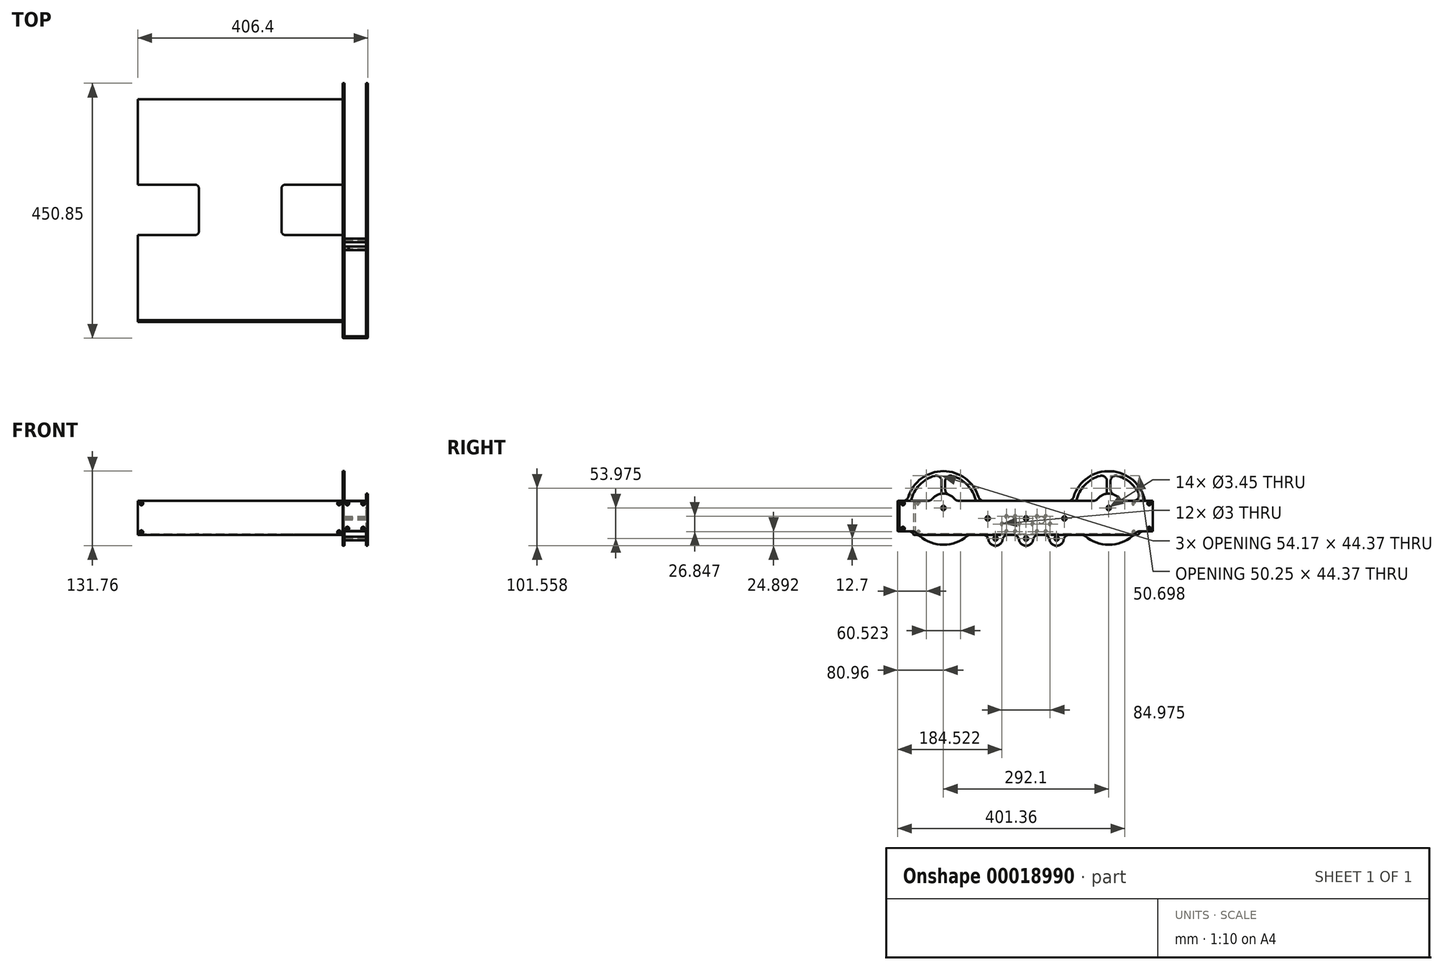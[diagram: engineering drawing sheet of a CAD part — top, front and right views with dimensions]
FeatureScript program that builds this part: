
annotation { "Feature Type Name" : "Feature", "Feature Type Description" : "" }
export const myFeature = defineFeature(function(context is Context, id is Id, definition is map)
    precondition{}
    {
        {
            var Q0;
            Q0=qCreatedBy(makeId("Right.planeOp"),FACE);
            var sketch = newSketch(context, id + "F0", { "sketchPlane" : qUnion([Q0])});
            skLineSegment(sketch, "E0", {"start": v(-222.25, 0) * mm, "end": v(222.25, 0) * mm});
            skCircle(sketch, "E1", {"center": v(-146.05, 79.38) * mm, "radius": 76.2 * mm});
            skCircle(sketch, "E2", {"center": v(-53.98, 25.4) * mm, "radius": 25.4 * mm});
            skCircle(sketch, "E3", {"center": v(53.98, 25.4) * mm, "radius": 25.4 * mm});
            skCircle(sketch, "E4", {"center": v(146.05, 79.38) * mm, "radius": 76.2 * mm});
            skLineSegment(sketch, "E5", {"start": v(0, 0) * mm, "end": v(0, 444.5) * mm, "construction": true});
            skLineSegment(sketch, "E6", {"start": v(222.25, 0) * mm, "end": v(222.25, 444.5) * mm, "construction": true});
            skCircle(sketch, "E7", {"center": v(0, 25.4) * mm, "radius": 25.4 * mm});
            skCircle(sketch, "E8", {"center": v(-146.05, 79.38) * mm, "radius": 63.5 * mm, "construction": true});
            skCircle(sketch, "E9", {"center": v(-53.98, 25.4) * mm, "radius": 21.17 * mm, "construction": true});
            skCircle(sketch, "E10", {"center": v(0, 25.4) * mm, "radius": 21.17 * mm, "construction": true});
            skCircle(sketch, "E11", {"center": v(53.98, 25.4) * mm, "radius": 21.17 * mm, "construction": true});
            skCircle(sketch, "E12", {"center": v(-67.76, 60.92) * mm, "radius": 16.93 * mm, "construction": true});
            skCircle(sketch, "E13", {"center": v(146.05, 79.38) * mm, "radius": 63.5 * mm, "construction": true});
            skCircle(sketch, "E14", {"center": v(-26.99, 58.02) * mm, "radius": 21.17 * mm, "construction": true});
            skCircle(sketch, "E15", {"center": v(26.99, 58.02) * mm, "radius": 21.17 * mm, "construction": true});
            skCircle(sketch, "E16", {"center": v(-67.76, 60.92) * mm, "radius": 3.18 * mm, "construction": true});
            skCircle(sketch, "E17", {"center": v(-67.76, 60.92) * mm, "radius": 18 * mm, "construction": true});
            skCircle(sketch, "E18", {"center": v(-26.99, 58.02) * mm, "radius": 22.23 * mm, "construction": true});
            skCircle(sketch, "E19", {"center": v(67.76, 60.92) * mm, "radius": 16.93 * mm, "construction": true});
            skLineSegment(sketch, "E20", {"start": v(-222.25, 0) * mm, "end": v(-222.25, 444.5) * mm, "construction": true});
            skSolve(sketch);
        }
        {
            var Q0;
            Q0=qCreatedBy(makeId("Right.planeOp"),FACE);
            var sketch = newSketch(context, id + "F1", { "sketchPlane" : qUnion([Q0])});
            skPoint(sketch, "E21.0", {"position": v(-146.05, 79.38) * mm});
            skPoint(sketch, "E21.1", {"position": v(-53.98, 25.4) * mm});
            skPoint(sketch, "E21.2", {"position": v(0, 25.4) * mm});
            skPoint(sketch, "E21.3", {"position": v(53.98, 25.4) * mm});
            skPoint(sketch, "E21.4", {"position": v(146.05, 79.38) * mm});
            skPoint(sketch, "E21.5", {"position": v(67.76, 60.92) * mm});
            skPoint(sketch, "E21.6", {"position": v(26.99, 58.02) * mm});
            skPoint(sketch, "E21.7", {"position": v(-26.99, 58.02) * mm});
            skPoint(sketch, "E21.8", {"position": v(-67.76, 60.92) * mm});
            skArc(sketch, "E22", {"start": v(42.98, 31.75) * mm, "mid": v(53.98, 12.7) * mm, "end": v(64.97, 31.75) * mm});
            skArc(sketch, "E23", {"start": v(-11, 31.75) * mm, "mid": v(0, 12.7) * mm, "end": v(11, 31.75) * mm});
            skArc(sketch, "E24", {"start": v(-64.97, 31.75) * mm, "mid": v(-53.98, 12.7) * mm, "end": v(-42.98, 31.75) * mm});
            skLineSegment(sketch, "E25", {"start": v(42.98, 31.75) * mm, "end": v(11, 31.75) * mm});
            skLineSegment(sketch, "E26", {"start": v(-11, 31.75) * mm, "end": v(-42.98, 31.75) * mm});
            skPoint(sketch, "E27", {"position": v(0, 60.92) * mm});
            skLineSegment(sketch, "E28", {"start": v(101.69, 31.75) * mm, "end": v(64.97, 31.75) * mm});
            skLineSegment(sketch, "E29", {"start": v(-198.44, 38.1) * mm, "end": v(-223.84, 38.1) * mm});
            skLineSegment(sketch, "E30", {"start": v(-223.84, 38.1) * mm, "end": v(-223.84, 92.08) * mm});
            skLineSegment(sketch, "E31", {"start": v(198.44, 38.1) * mm, "end": v(223.84, 38.1) * mm});
            skLineSegment(sketch, "E32", {"start": v(223.84, 38.1) * mm, "end": v(223.84, 92.08) * mm});
            skArc(sketch, "E33.trimOffspring", {"start": v(-190.41, 31.75) * mm, "mid": v(-146.05, 14.29) * mm, "end": v(-101.69, 31.75) * mm});
            skLineSegment(sketch, "E34.trimOffspring", {"start": v(-223.84, 92.08) * mm, "end": v(-168.05, 92.08) * mm});
            skCircle(sketch, "E35", {"center": v(0, 25.4) * mm, "radius": 3.9 * mm, "construction": true});
            skLineSegment(sketch, "E36.trimOffspring", {"start": v(-64.97, 31.75) * mm, "end": v(-101.69, 31.75) * mm});
            skArc(sketch, "E37.trimOffspring", {"start": v(101.69, 31.75) * mm, "mid": v(146.05, 14.29) * mm, "end": v(190.41, 31.75) * mm});
            skArc(sketch, "E38", {"start": v(-124.05, 92.08) * mm, "mid": v(-146.05, 104.78) * mm, "end": v(-168.05, 92.08) * mm});
            skArc(sketch, "E39", {"start": v(168.05, 92.08) * mm, "mid": v(146.05, 104.78) * mm, "end": v(124.05, 92.08) * mm});
            skLineSegment(sketch, "E40.trimOffspring", {"start": v(-124.05, 92.08) * mm, "end": v(124.05, 92.08) * mm});
            skLineSegment(sketch, "E41.trimOffspring", {"start": v(168.05, 92.08) * mm, "end": v(223.84, 92.08) * mm});
            skLineSegment(sketch, "E42", {"start": v(-190.41, 31.75) * mm, "end": v(-198.44, 31.75) * mm});
            skLineSegment(sketch, "E43", {"start": v(-198.44, 31.75) * mm, "end": v(-198.44, 38.1) * mm});
            skLineSegment(sketch, "E44", {"start": v(190.41, 31.75) * mm, "end": v(198.44, 31.75) * mm});
            skLineSegment(sketch, "E45", {"start": v(198.44, 31.75) * mm, "end": v(198.44, 38.1) * mm});
            skSolve(sketch);
        }
        {
            var Q0;
            Q0 = qSketchRegion(id + "F1", true);
            extrude(context, id + "F2", {"entities" : qUnion([Q0]), "depth" : 3.17 * mm});
        }
        {
            var Q0;
            Q0=makeQuery(id+"F2.opExtrude","SWEPT_EDGE",EDGE,{"disambiguationData":[OSD([sQuery(id+"F1.wireOp",EDGE,"E28"),sQuery(id+"F1.wireOp",EDGE,"E37.trimOffspring")])]});
            var Q1;
            Q1=makeQuery(id+"F2.opExtrude","SWEPT_EDGE",EDGE,{"disambiguationData":[OSD([sQuery(id+"F1.wireOp",EDGE,"E31"),sQuery(id+"F1.wireOp",EDGE,"E45")])]});
            var Q2;
            Q2=makeQuery(id+"F2.opExtrude","SWEPT_EDGE",EDGE,{"disambiguationData":[OSD([sQuery(id+"F1.wireOp",EDGE,"E37.trimOffspring"),sQuery(id+"F1.wireOp",EDGE,"E44")])]});
            var Q3;
            Q3=makeQuery(id+"F2.opExtrude","SWEPT_EDGE",EDGE,{"disambiguationData":[OSD([sQuery(id+"F1.wireOp",EDGE,"E24"),sQuery(id+"F1.wireOp",EDGE,"E36.trimOffspring")])]});
            var Q4;
            Q4=makeQuery(id+"F2.opExtrude","SWEPT_EDGE",EDGE,{"disambiguationData":[OSD([sQuery(id+"F1.wireOp",EDGE,"E24"),sQuery(id+"F1.wireOp",EDGE,"E26")])]});
            var Q5;
            Q5=makeQuery(id+"F2.opExtrude","SWEPT_EDGE",EDGE,{"disambiguationData":[OSD([sQuery(id+"F1.wireOp",EDGE,"E24"),sQuery(id+"F1.wireOp",EDGE,"E26")])]});
            var Q6;
            Q6=makeQuery(id+"F2.opExtrude","SWEPT_EDGE",EDGE,{"disambiguationData":[OSD([sQuery(id+"F1.wireOp",EDGE,"E23"),sQuery(id+"F1.wireOp",EDGE,"E26")])]});
            var Q7;
            Q7=makeQuery(id+"F2.opExtrude","SWEPT_EDGE",EDGE,{"disambiguationData":[OSD([sQuery(id+"F1.wireOp",EDGE,"E23"),sQuery(id+"F1.wireOp",EDGE,"E25")])]});
            var Q8;
            Q8=makeQuery(id+"F2.opExtrude","SWEPT_EDGE",EDGE,{"disambiguationData":[OSD([sQuery(id+"F1.wireOp",EDGE,"E22"),sQuery(id+"F1.wireOp",EDGE,"E25")])]});
            var Q9;
            Q9=makeQuery(id+"F2.opExtrude","SWEPT_EDGE",EDGE,{"disambiguationData":[OSD([sQuery(id+"F1.wireOp",EDGE,"E22"),sQuery(id+"F1.wireOp",EDGE,"E28")])]});
            var Q10;
            Q10=makeQuery(id+"F2.opExtrude","SWEPT_EDGE",EDGE,{"disambiguationData":[OSD([sQuery(id+"F1.wireOp",EDGE,"E22"),sQuery(id+"F1.wireOp",EDGE,"E25")])]});
            var Q11;
            Q11=makeQuery(id+"F2.opExtrude","SWEPT_EDGE",EDGE,{"disambiguationData":[OSD([sQuery(id+"F1.wireOp",EDGE,"E33.trimOffspring"),sQuery(id+"F1.wireOp",EDGE,"E36.trimOffspring")])]});
            var Q12;
            Q12=makeQuery(id+"F2.opExtrude","SWEPT_EDGE",EDGE,{"disambiguationData":[OSD([sQuery(id+"F1.wireOp",EDGE,"E29"),sQuery(id+"F1.wireOp",EDGE,"E43")])]});
            var Q13;
            Q13=makeQuery(id+"F2.opExtrude","SWEPT_EDGE",EDGE,{"disambiguationData":[OSD([sQuery(id+"F1.wireOp",EDGE,"E33.trimOffspring"),sQuery(id+"F1.wireOp",EDGE,"E42")])]});
            var Q14;
            Q14=makeQuery(id+"F2.opExtrude","SWEPT_EDGE",EDGE,{"disambiguationData":[OSD([sQuery(id+"F1.wireOp",EDGE,"E33.trimOffspring"),sQuery(id+"F1.wireOp",EDGE,"E36.trimOffspring")])]});
            var Q15;
            Q15=makeQuery(id+"F2.opExtrude","SWEPT_EDGE",EDGE,{"disambiguationData":[OSD([sQuery(id+"F1.wireOp",EDGE,"E28"),sQuery(id+"F1.wireOp",EDGE,"E37.trimOffspring")])]});
            var Q16;
            Q16=makeQuery(id+"F2.opExtrude","SWEPT_EDGE",EDGE,{"disambiguationData":[OSD([sQuery(id+"F1.wireOp",EDGE,"E34.trimOffspring"),sQuery(id+"F1.wireOp",EDGE,"E38")])]});
            var Q17;
            Q17=makeQuery(id+"F2.opExtrude","SWEPT_EDGE",EDGE,{"disambiguationData":[OSD([sQuery(id+"F1.wireOp",EDGE,"E38"),sQuery(id+"F1.wireOp",EDGE,"E40.trimOffspring")])]});
            var Q18;
            Q18=makeQuery(id+"F2.opExtrude","SWEPT_EDGE",EDGE,{"disambiguationData":[OSD([sQuery(id+"F1.wireOp",EDGE,"E39"),sQuery(id+"F1.wireOp",EDGE,"E40.trimOffspring")])]});
            var Q19;
            Q19=makeQuery(id+"F2.opExtrude","SWEPT_EDGE",EDGE,{"disambiguationData":[OSD([sQuery(id+"F1.wireOp",EDGE,"E39"),sQuery(id+"F1.wireOp",EDGE,"E41.trimOffspring")])]});
            fillet(context, id + "F3", {"entities" : qUnion([Q0, Q1, Q2, Q3, Q4, Q5, Q6, Q7, Q8, Q9, Q10, Q11, Q12, Q13, Q14, Q15, Q16, Q17, Q18, Q19]), "radius" : 9.52 * mm, "tangentPropagation" : true, "allowEdgeOverflow" : false});
        }
        {
            var Q0;
            Q0=sQuery(id+"F0.wireOp",VERTEX,"E1.center");
            var Q1;
            Q1=sQuery(id+"F0.wireOp",VERTEX,"E16.center");
            var Q2;
            Q2=sQuery(id+"F0.wireOp",VERTEX,"E2.center");
            var Q3;
            Q3=sQuery(id+"F0.wireOp",VERTEX,"E7.center");
            var Q4;
            Q4=sQuery(id+"F0.wireOp",VERTEX,"E11.center");
            var Q5;
            Q5=sQuery(id+"F0.wireOp",VERTEX,"E13.center");
            var Q6;
            Q6=sQuery(id+"F0.wireOp",VERTEX,"E19.center");
            var Q7;
            Q7=sQuery(id+"F1.wireOp",VERTEX,"E27");
            var Q8;
            Q8=makeQuery(id+"F2.opExtrude","SWEPT_BODY",BODY,{"disambiguationData":[OSD([sQuery(id+"F1.wireOp",EDGE,"15da93e0-f6f9-46fd-b5b2-a4333d812dff"),sQuery(id+"F1.wireOp",EDGE,"16e28298-e9de-4e3e-a815-65364f24cef6"),sQuery(id+"F1.wireOp",EDGE,"E22"),sQuery(id+"F1.wireOp",EDGE,"E23"),sQuery(id+"F1.wireOp",EDGE,"E24"),sQuery(id+"F1.wireOp",EDGE,"E25"),sQuery(id+"F1.wireOp",EDGE,"E26"),sQuery(id+"F1.wireOp",EDGE,"859b3a9e-47a0-477d-ad96-80d0cd043ae0"),sQuery(id+"F1.wireOp",EDGE,"689f9d55-c2b5-4ecb-a3d1-7254dc2b26e6"),sQuery(id+"F1.wireOp",EDGE,"4789f967-c616-4e3b-9a4c-ef86a0a08756")])]});
            hole(context, id + "F4", {"style" : HoleStyle.SIMPLE, "holeDiameter" : 3.45 * mm, "endStyle" : HoleEndStyle.THROUGH, "oppositeDirection" : true, "locations" : qUnion([Q0, Q1, Q2, Q3, Q4, Q5, Q6, Q7]), "scope" : qUnion([Q8])});
        }
        {
            var Q0;
            Q0=sQuery(id+"F1.wireOp",VERTEX,"E21.4");
            var Q1;
            Q1=sQuery(id+"F1.wireOp",VERTEX,"E21.0");
            var Q2;
            Q2=makeQuery(id+"F2.opExtrude","SWEPT_BODY",BODY,{"disambiguationData":[OSD([sQuery(id+"F1.wireOp",EDGE,"E22"),sQuery(id+"F1.wireOp",EDGE,"E23"),sQuery(id+"F1.wireOp",EDGE,"E24"),sQuery(id+"F1.wireOp",EDGE,"E25"),sQuery(id+"F1.wireOp",EDGE,"E26"),sQuery(id+"F1.wireOp",EDGE,"E28"),sQuery(id+"F1.wireOp",EDGE,"E29"),sQuery(id+"F1.wireOp",EDGE,"E30"),sQuery(id+"F1.wireOp",EDGE,"E31"),sQuery(id+"F1.wireOp",EDGE,"E32"),sQuery(id+"F1.wireOp",EDGE,"E33.trimOffspring"),sQuery(id+"F1.wireOp",EDGE,"E34.trimOffspring"),sQuery(id+"F1.wireOp",EDGE,"E36.trimOffspring"),sQuery(id+"F1.wireOp",EDGE,"E37.trimOffspring"),sQuery(id+"F1.wireOp",EDGE,"E38"),sQuery(id+"F1.wireOp",EDGE,"E39"),sQuery(id+"F1.wireOp",EDGE,"E40.trimOffspring"),sQuery(id+"F1.wireOp",EDGE,"E41.trimOffspring"),sQuery(id+"F1.wireOp",EDGE,"E42"),sQuery(id+"F1.wireOp",EDGE,"E43"),sQuery(id+"F1.wireOp",EDGE,"E44"),sQuery(id+"F1.wireOp",EDGE,"E45")])]});
            hole(context, id + "F5", {"style" : HoleStyle.SIMPLE, "holeDiameter" : 4.76 * mm, "endStyle" : HoleEndStyle.THROUGH, "oppositeDirection" : true, "locations" : qUnion([Q0, Q1]), "scope" : qUnion([Q2])});
        }
        {
            var Q0;
            Q0=makeQuery(id+"F2.opExtrude","CAP_FACE",FACE,{"disambiguationData":[OSD([sQuery(id+"F1.wireOp",EDGE,"15da93e0-f6f9-46fd-b5b2-a4333d812dff"),sQuery(id+"F1.wireOp",EDGE,"16e28298-e9de-4e3e-a815-65364f24cef6"),sQuery(id+"F1.wireOp",EDGE,"E22"),sQuery(id+"F1.wireOp",EDGE,"E23"),sQuery(id+"F1.wireOp",EDGE,"E24"),sQuery(id+"F1.wireOp",EDGE,"E25"),sQuery(id+"F1.wireOp",EDGE,"E26"),sQuery(id+"F1.wireOp",EDGE,"859b3a9e-47a0-477d-ad96-80d0cd043ae0"),sQuery(id+"F1.wireOp",EDGE,"689f9d55-c2b5-4ecb-a3d1-7254dc2b26e6"),sQuery(id+"F1.wireOp",EDGE,"4789f967-c616-4e3b-9a4c-ef86a0a08756")])],"isStart":false});
            var sketch = newSketch(context, id + "F6", { "sketchPlane" : qUnion([Q0])});
            skCircle(sketch, "E46", {"center": v(-26.99, 51.02) * mm, "radius": 18.5 * mm, "construction": true});
            skCircle(sketch, "E47", {"center": v(-26.99, 58.02) * mm, "radius": 6 * mm});
            skCircle(sketch, "E48.cCircle", {"center": v(-26.99, 51.02) * mm, "radius": 15.5 * mm, "construction": true});
            skLineSegment(sketch, "E48.0", {"start": v(-11.49, 51.02) * mm, "end": v(-19.24, 37.6) * mm, "construction": true});
            skLineSegment(sketch, "E48.1", {"start": v(-19.24, 37.6) * mm, "end": v(-34.74, 37.6) * mm, "construction": true});
            skLineSegment(sketch, "E48.2", {"start": v(-34.74, 37.6) * mm, "end": v(-42.49, 51.02) * mm, "construction": true});
            skLineSegment(sketch, "E48.3", {"start": v(-42.49, 51.02) * mm, "end": v(-34.74, 64.44) * mm, "construction": true});
            skLineSegment(sketch, "E48.4", {"start": v(-34.74, 64.44) * mm, "end": v(-19.24, 64.44) * mm, "construction": true});
            skLineSegment(sketch, "E48.5", {"start": v(-19.24, 64.44) * mm, "end": v(-11.49, 51.02) * mm, "construction": true});
            skCircle(sketch, "E49.MirrorC", {"center": v(26.99, 58.02) * mm, "radius": 6 * mm});
            skLineSegment(sketch, "E50.MirrorCS", {"start": v(19.24, 64.44) * mm, "end": v(11.49, 51.02) * mm, "construction": true});
            skLineSegment(sketch, "E51.MirrorCS", {"start": v(11.49, 51.02) * mm, "end": v(19.24, 37.6) * mm, "construction": true});
            skLineSegment(sketch, "E52.MirrorCS", {"start": v(19.24, 37.6) * mm, "end": v(34.74, 37.6) * mm, "construction": true});
            skLineSegment(sketch, "E53.MirrorCS", {"start": v(34.74, 37.6) * mm, "end": v(42.49, 51.02) * mm, "construction": true});
            skLineSegment(sketch, "E54.MirrorCS", {"start": v(42.49, 51.02) * mm, "end": v(34.74, 64.44) * mm, "construction": true});
            skLineSegment(sketch, "E55.MirrorCS", {"start": v(34.74, 64.44) * mm, "end": v(19.24, 64.44) * mm, "construction": true});
            skSolve(sketch);
        }
        {
            var Q0;
            Q0 = qSketchRegion(id + "F6", true);
            extrude(context, id + "F7", {"entities" : qUnion([Q0]), "operationType" : NewBodyOperationType.REMOVE, "endBound" : BoundingType.UP_TO_NEXT, "oppositeDirection" : true, "depth" : 25.4 * mm});
        }
        {
            var Q0;
            Q0=sQuery(id+"F6.wireOp",VERTEX,"E48.4.start");
            var Q1;
            Q1=sQuery(id+"F6.wireOp",VERTEX,"E48.2.end");
            var Q2;
            Q2=sQuery(id+"F6.wireOp",VERTEX,"E48.2.start");
            var Q3;
            Q3=sQuery(id+"F6.wireOp",VERTEX,"E48.0.end");
            var Q4;
            Q4=sQuery(id+"F6.wireOp",VERTEX,"E48.5.end");
            var Q5;
            Q5=sQuery(id+"F6.wireOp",VERTEX,"E48.5.start");
            var Q6;
            Q6=sQuery(id+"F6.wireOp",VERTEX,"E51.MirrorCS.start");
            var Q7;
            Q7=sQuery(id+"F6.wireOp",VERTEX,"E55.MirrorCS.end");
            var Q8;
            Q8=sQuery(id+"F6.wireOp",VERTEX,"E54.MirrorCS.end");
            var Q9;
            Q9=sQuery(id+"F6.wireOp",VERTEX,"E54.MirrorCS.start");
            var Q10;
            Q10=sQuery(id+"F6.wireOp",VERTEX,"E52.MirrorCS.end");
            var Q11;
            Q11=sQuery(id+"F6.wireOp",VERTEX,"E51.MirrorCS.end");
            var Q12;
            Q12=makeQuery(id+"F2.opExtrude","SWEPT_BODY",BODY,{"disambiguationData":[OSD([sQuery(id+"F1.wireOp",EDGE,"15da93e0-f6f9-46fd-b5b2-a4333d812dff"),sQuery(id+"F1.wireOp",EDGE,"16e28298-e9de-4e3e-a815-65364f24cef6"),sQuery(id+"F1.wireOp",EDGE,"E22"),sQuery(id+"F1.wireOp",EDGE,"E23"),sQuery(id+"F1.wireOp",EDGE,"E24"),sQuery(id+"F1.wireOp",EDGE,"E25"),sQuery(id+"F1.wireOp",EDGE,"E26"),sQuery(id+"F1.wireOp",EDGE,"859b3a9e-47a0-477d-ad96-80d0cd043ae0"),sQuery(id+"F1.wireOp",EDGE,"689f9d55-c2b5-4ecb-a3d1-7254dc2b26e6"),sQuery(id+"F1.wireOp",EDGE,"4789f967-c616-4e3b-9a4c-ef86a0a08756")])]});
            hole(context, id + "F8", {"style" : HoleStyle.C_SINK, "holeDiameter" : 3 * mm, "cSinkDiameter" : 6 * mm, "endStyle" : HoleEndStyle.THROUGH, "locations" : qUnion([Q0, Q1, Q2, Q3, Q4, Q5, Q6, Q7, Q8, Q9, Q10, Q11]), "scope" : qUnion([Q12]), "cSinkAngle" : 90 * degree});
        }
        {
            var Q0;
            Q0=makeQuery(id+"F6.imprint","IMPRINT",FACE,{"disambiguationData":[TD([[makeQuery(id+"F6.imprint","IMPRINT",EDGE,{"derivedFrom":sQuery(id+"F6.wireOp",EDGE,"E47")}),-1.0]])]});
            cPlane(context, id + "F9", {"entities" : qUnion([Q0]), "cplaneType" : CPlaneType.OFFSET, "offset" : 38.1 * mm, "width" : 152.4 * mm, "height" : 152.4 * mm});
        }
        {
            var Q0;
            Q0=qCreatedBy(id+"F9.planeOp",FACE);
            var sketch = newSketch(context, id + "F10", { "sketchPlane" : qUnion([Q0])});
            skArc(sketch, "E56.0.5", {"start": v(-66.54, 23.59) * mm, "mid": v(-53.98, 12.7) * mm, "end": v(-41.4, 23.59) * mm});
            skArc(sketch, "E56.0.6", {"start": v(-41.4, 23.59) * mm, "mid": v(-38.21, 29.43) * mm, "end": v(-31.98, 31.75) * mm});
            skLineSegment(sketch, "E56.0.7", {"start": v(-31.98, 31.75) * mm, "end": v(-22, 31.75) * mm});
            skArc(sketch, "E56.0.8", {"start": v(-22, 31.75) * mm, "mid": v(-15.76, 29.43) * mm, "end": v(-12.57, 23.59) * mm});
            skArc(sketch, "E56.0.9", {"start": v(-12.57, 23.59) * mm, "mid": v(0, 12.7) * mm, "end": v(12.57, 23.59) * mm});
            skArc(sketch, "E56.0.10", {"start": v(12.57, 23.59) * mm, "mid": v(15.76, 29.43) * mm, "end": v(22, 31.75) * mm});
            skLineSegment(sketch, "E56.0.11", {"start": v(22, 31.75) * mm, "end": v(31.98, 31.75) * mm});
            skArc(sketch, "E56.0.12", {"start": v(31.98, 31.75) * mm, "mid": v(38.21, 29.43) * mm, "end": v(41.4, 23.59) * mm});
            skLineSegment(sketch, "E56.0.14", {"start": v(41.4, 23.59) * mm, "end": v(41.4, 23.59) * mm});
            skCircle(sketch, "E57.0", {"center": v(-146.05, 79.38) * mm, "radius": 1.73 * mm});
            skCircle(sketch, "E57.1", {"center": v(-53.98, 25.4) * mm, "radius": 1.73 * mm});
            skCircle(sketch, "E57.2", {"center": v(0, 25.4) * mm, "radius": 1.73 * mm});
            skCircle(sketch, "E57.3", {"center": v(-67.76, 60.92) * mm, "radius": 1.73 * mm});
            skCircle(sketch, "E57.4", {"center": v(53.98, 25.4) * mm, "radius": 1.73 * mm});
            skCircle(sketch, "E57.5", {"center": v(146.05, 79.38) * mm, "radius": 1.73 * mm});
            skCircle(sketch, "E58.0", {"center": v(67.76, 60.92) * mm, "radius": 1.73 * mm});
            skArc(sketch, "E59.0", {"start": v(-75.97, 31.75) * mm, "mid": v(-69.74, 29.43) * mm, "end": v(-66.54, 23.59) * mm});
            skLineSegment(sketch, "E59.1", {"start": v(-75.97, 31.75) * mm, "end": v(-190.41, 31.75) * mm});
            skArc(sketch, "E59.3", {"start": v(-196.38, 38.1) * mm, "mid": v(-193.5, 34.83) * mm, "end": v(-190.41, 31.75) * mm});
            skLineSegment(sketch, "E59.5", {"start": v(-196.38, 38.1) * mm, "end": v(-223.84, 38.1) * mm});
            skLineSegment(sketch, "E59.6", {"start": v(-223.84, 38.1) * mm, "end": v(-223.84, 92.08) * mm});
            skLineSegment(sketch, "E59.7", {"start": v(-223.84, 92.08) * mm, "end": v(-223.84, 92.08) * mm});
            skArc(sketch, "E59.8", {"start": v(41.4, 23.59) * mm, "mid": v(53.98, 12.7) * mm, "end": v(66.54, 23.59) * mm});
            skArc(sketch, "E59.9", {"start": v(66.54, 23.59) * mm, "mid": v(69.74, 29.43) * mm, "end": v(75.97, 31.75) * mm});
            skLineSegment(sketch, "E59.10", {"start": v(190.41, 31.75) * mm, "end": v(75.97, 31.75) * mm});
            skArc(sketch, "E59.12", {"start": v(190.41, 31.75) * mm, "mid": v(193.5, 34.83) * mm, "end": v(196.38, 38.1) * mm});
            skLineSegment(sketch, "E60.0", {"start": v(173, 92.08) * mm, "end": v(223.84, 92.08) * mm});
            skArc(sketch, "E60.1", {"start": v(165.64, 95.54) * mm, "mid": v(168.93, 92.98) * mm, "end": v(173, 92.08) * mm});
            skArc(sketch, "E60.2", {"start": v(165.64, 95.54) * mm, "mid": v(146.05, 104.78) * mm, "end": v(126.46, 95.54) * mm});
            skArc(sketch, "E61.0", {"start": v(126.46, 95.54) * mm, "mid": v(123.17, 92.98) * mm, "end": v(119.1, 92.08) * mm});
            skLineSegment(sketch, "E61.1", {"start": v(-119.1, 92.08) * mm, "end": v(119.1, 92.08) * mm});
            skArc(sketch, "E61.2", {"start": v(-119.1, 92.08) * mm, "mid": v(-123.17, 92.98) * mm, "end": v(-126.46, 95.54) * mm});
            skArc(sketch, "E61.3", {"start": v(-126.46, 95.54) * mm, "mid": v(-146.05, 104.78) * mm, "end": v(-165.64, 95.54) * mm});
            skArc(sketch, "E61.4", {"start": v(-165.64, 95.54) * mm, "mid": v(-168.93, 92.98) * mm, "end": v(-173, 92.08) * mm});
            skLineSegment(sketch, "E61.5", {"start": v(-223.84, 92.08) * mm, "end": v(-173, 92.08) * mm});
            skLineSegment(sketch, "E62.0", {"start": v(223.84, 38.1) * mm, "end": v(223.84, 92.08) * mm});
            skLineSegment(sketch, "E62.1", {"start": v(196.38, 38.1) * mm, "end": v(223.84, 38.1) * mm});
            skSolve(sketch);
        }
        {
            var Q0;
            Q0 = qSketchRegion(id + "F10", true);
            extrude(context, id + "F11", {"entities" : qUnion([Q0]), "depth" : 3.17 * mm});
        }
        {
            var Q0;
            Q0=makeQuery(id+"F11.opExtrude","SWEPT_EDGE",EDGE,{"disambiguationData":[OSD([sQuery(id+"F10.wireOp",EDGE,"E59.3"),sQuery(id+"F10.wireOp",EDGE,"E59.5")])]});
            var Q1;
            Q1=makeQuery(id+"F11.opExtrude","SWEPT_EDGE",EDGE,{"disambiguationData":[OSD([sQuery(id+"F10.wireOp",EDGE,"E59.12"),sQuery(id+"F10.wireOp",EDGE,"E62.1")])]});
            var Q2;
            Q2=makeQuery(id+"F11.opExtrude","SWEPT_EDGE",EDGE,{"disambiguationData":[OSD([sQuery(id+"F10.wireOp",EDGE,"E59.1"),sQuery(id+"F10.wireOp",EDGE,"E59.3")])]});
            var Q3;
            Q3=makeQuery(id+"F11.opExtrude","SWEPT_EDGE",EDGE,{"disambiguationData":[OSD([sQuery(id+"F10.wireOp",EDGE,"E59.10"),sQuery(id+"F10.wireOp",EDGE,"E59.12")])]});
            fillet(context, id + "F12", {"entities" : qUnion([Q0, Q1, Q2, Q3]), "radius" : 9.52 * mm, "tangentPropagation" : true, "allowEdgeOverflow" : false});
        }
        {
            var Q0;
            Q0=makeQuery(id+"F2.opExtrude","CAP_FACE",FACE,{"disambiguationData":[OSD([sQuery(id+"F1.wireOp",EDGE,"15da93e0-f6f9-46fd-b5b2-a4333d812dff"),sQuery(id+"F1.wireOp",EDGE,"16e28298-e9de-4e3e-a815-65364f24cef6"),sQuery(id+"F1.wireOp",EDGE,"E22"),sQuery(id+"F1.wireOp",EDGE,"E23"),sQuery(id+"F1.wireOp",EDGE,"E24"),sQuery(id+"F1.wireOp",EDGE,"E25"),sQuery(id+"F1.wireOp",EDGE,"E26"),sQuery(id+"F1.wireOp",EDGE,"859b3a9e-47a0-477d-ad96-80d0cd043ae0"),sQuery(id+"F1.wireOp",EDGE,"689f9d55-c2b5-4ecb-a3d1-7254dc2b26e6"),sQuery(id+"F1.wireOp",EDGE,"4789f967-c616-4e3b-9a4c-ef86a0a08756")])],"isStart":true});
            var sketch = newSketch(context, id + "F13", { "sketchPlane" : qUnion([Q0])});
            skCircle(sketch, "E63.cCircle", {"center": v(86.38, 21.35) * mm, "radius": 6.35 * mm, "construction": true});
            skLineSegment(sketch, "E63.0", {"start": v(82.72, 27.7) * mm, "end": v(90.05, 27.7) * mm});
            skLineSegment(sketch, "E63.1", {"start": v(90.05, 27.7) * mm, "end": v(93.71, 21.35) * mm});
            skLineSegment(sketch, "E63.2", {"start": v(93.71, 21.35) * mm, "end": v(90.05, 15) * mm});
            skLineSegment(sketch, "E63.3", {"start": v(90.05, 15) * mm, "end": v(82.72, 15) * mm});
            skLineSegment(sketch, "E63.4", {"start": v(82.72, 15) * mm, "end": v(79.05, 21.35) * mm});
            skLineSegment(sketch, "E63.5", {"start": v(79.05, 21.35) * mm, "end": v(82.72, 27.7) * mm});
            skPoint(sketch, "E63.0.midPoint", {"position": v(86.38, 27.7) * mm});
            skCircle(sketch, "E64.cCircle", {"center": v(26.99, 8.64) * mm, "radius": 6.35 * mm, "construction": true});
            skLineSegment(sketch, "E64.0", {"start": v(23.32, 15) * mm, "end": v(30.65, 15) * mm});
            skLineSegment(sketch, "E64.1", {"start": v(30.65, 15) * mm, "end": v(34.32, 8.64) * mm});
            skLineSegment(sketch, "E64.2", {"start": v(34.32, 8.64) * mm, "end": v(30.65, 2.3) * mm});
            skLineSegment(sketch, "E64.3", {"start": v(30.65, 2.3) * mm, "end": v(23.32, 2.3) * mm});
            skLineSegment(sketch, "E64.4", {"start": v(23.32, 2.3) * mm, "end": v(19.66, 8.64) * mm});
            skLineSegment(sketch, "E64.5", {"start": v(19.66, 8.64) * mm, "end": v(23.32, 15) * mm});
            skPoint(sketch, "E64.0.midPoint", {"position": v(26.99, 15) * mm});
            skCircle(sketch, "E65.cCircle", {"center": v(210.2, 26.67) * mm, "radius": 6.35 * mm, "construction": true});
            skLineSegment(sketch, "E65.0", {"start": v(206.53, 33.02) * mm, "end": v(213.86, 33.02) * mm});
            skLineSegment(sketch, "E65.1", {"start": v(213.86, 33.02) * mm, "end": v(217.53, 26.67) * mm});
            skLineSegment(sketch, "E65.2", {"start": v(217.53, 26.67) * mm, "end": v(213.86, 20.32) * mm});
            skLineSegment(sketch, "E65.3", {"start": v(213.86, 20.32) * mm, "end": v(206.53, 20.32) * mm});
            skLineSegment(sketch, "E65.4", {"start": v(206.53, 20.32) * mm, "end": v(202.86, 26.67) * mm});
            skLineSegment(sketch, "E65.5", {"start": v(202.86, 26.67) * mm, "end": v(206.53, 33.02) * mm});
            skPoint(sketch, "E65.0.midPoint", {"position": v(210.2, 33.02) * mm});
            skLineSegment(sketch, "E66.bottom", {"start": v(236.09, 0) * mm, "end": v(286.89, 0) * mm});
            skLineSegment(sketch, "E66.top", {"start": v(236.09, 50.8) * mm, "end": v(286.89, 50.8) * mm});
            skLineSegment(sketch, "E66.left", {"start": v(236.09, 0) * mm, "end": v(236.09, 50.8) * mm});
            skLineSegment(sketch, "E66.right", {"start": v(286.89, 0) * mm, "end": v(286.89, 50.8) * mm});
            skCircle(sketch, "E67", {"center": v(265.1, 36.51) * mm, "radius": 36.51 * mm});
            skSolve(sketch);
        }
        {
            var Q0;
            Q0=makeQuery(id+"F6.imprint","IMPRINT",FACE,{"disambiguationData":[TD([[makeQuery(id+"F6.imprint","IMPRINT",EDGE,{"derivedFrom":sQuery(id+"F6.wireOp",EDGE,"E47")}),-1.0]])]});
            var sketch = newSketch(context, id + "F14", { "sketchPlane" : qUnion([Q0])});
            skCircle(sketch, "E68", {"center": v(-53.98, 25.4) * mm, "radius": 3.18 * mm});
            skLineSegment(sketch, "E69", {"start": v(-53.98, 25.4) * mm, "end": v(-67.76, 60.92) * mm, "construction": true});
            skCircle(sketch, "E70", {"center": v(-53.98, 25.4) * mm, "radius": 1.35 * mm});
            skSolve(sketch);
        }
        {
            var Q0;
            Q0=makeQuery(id+"F14.imprint","IMPRINT",FACE,{"disambiguationData":[TD([[makeQuery(id+"F14.imprint","IMPRINT",EDGE,{"derivedFrom":sQuery(id+"F14.wireOp",EDGE,"E70")}),-1.0]])]});
            var Q1;
            Q1=makeQuery(id+"F14.imprint","IMPRINT",FACE,{"disambiguationData":[TD([[makeQuery(id+"F14.imprint","IMPRINT",EDGE,{"derivedFrom":sQuery(id+"F14.wireOp",EDGE,"E68")}),1.0]])]});
            var Q2;
            Q2=makeQuery(id+"F11.opExtrude","CAP_FACE",FACE,{"disambiguationData":[OSD([sQuery(id+"F10.wireOp",EDGE,"E56.0.0"),sQuery(id+"F10.wireOp",EDGE,"E56.0.1"),sQuery(id+"F10.wireOp",EDGE,"E56.0.2"),sQuery(id+"F10.wireOp",EDGE,"E56.0.3"),sQuery(id+"F10.wireOp",EDGE,"E56.0.4"),sQuery(id+"F10.wireOp",EDGE,"E56.0.5"),sQuery(id+"F10.wireOp",EDGE,"E56.0.6"),sQuery(id+"F10.wireOp",EDGE,"E56.0.7"),sQuery(id+"F10.wireOp",EDGE,"E56.0.8"),sQuery(id+"F10.wireOp",EDGE,"E56.0.9"),sQuery(id+"F10.wireOp",EDGE,"E56.0.10"),sQuery(id+"F10.wireOp",EDGE,"E56.0.11"),sQuery(id+"F10.wireOp",EDGE,"E56.0.12"),sQuery(id+"F10.wireOp",EDGE,"E56.0.13"),sQuery(id+"F10.wireOp",EDGE,"E56.0.14"),sQuery(id+"F10.wireOp",EDGE,"E56.0.15"),sQuery(id+"F10.wireOp",EDGE,"E56.0.16"),sQuery(id+"F10.wireOp",EDGE,"E56.0.17"),sQuery(id+"F10.wireOp",EDGE,"E57.0"),sQuery(id+"F10.wireOp",EDGE,"E57.1"),sQuery(id+"F10.wireOp",EDGE,"E57.2"),sQuery(id+"F10.wireOp",EDGE,"E57.3"),sQuery(id+"F10.wireOp",EDGE,"E57.4"),sQuery(id+"F10.wireOp",EDGE,"E57.5"),sQuery(id+"F10.wireOp",EDGE,"E58.0")])],"isStart":true});
            extrude(context, id + "F15", {"entities" : qUnion([Q0, Q1]), "endBound" : BoundingType.UP_TO_SURFACE, "endBoundEntityFace" : qUnion([Q2]), "depth" : 25.4 * mm});
        }
        {
            var Q0;
            Q0=makeQuery(id+"F15.opExtrude","SWEPT_FACE",FACE,{"disambiguationData":[OSD([sQuery(id+"F14.wireOp",EDGE,"E68")])]});
            var Q1;
            Q1=makeQuery(id+"F15.opExtrude","SWEPT_FACE",FACE,{"disambiguationData":[OSD([sQuery(id+"F14.wireOp",EDGE,"1b7a65e0-1b23-40a1-a37a-c7c8615ee948.0")])]});
            chamfer(context, id + "F16", {"entities" : qUnion([Q0, Q1]), "width" : 0.25 * mm, "tangentPropagation" : true});
        }
        {
            var Q0;
            Q0=makeQuery(id+"F15.opExtrude","SWEPT_BODY",BODY,{"disambiguationData":[OSD([sQuery(id+"F14.wireOp",EDGE,"E68"),sQuery(id+"F14.wireOp",EDGE,"1b7a65e0-1b23-40a1-a37a-c7c8615ee948.0")])]});
            var Q1;
            Q1=sQuery(id+"F14.wireOp",EDGE,"E69");
            transform(context, id + "F17", {"entities" : qUnion([Q0]), "transformType" : TransformType.TRANSLATION_ENTITY, "oppositeDirectionEntity" : false, "transformLine" : qUnion([Q1]), "makeCopy" : true});
        }
        {
            var Q0;
            Q0=makeQuery(id+"F6.imprint","IMPRINT",FACE,{"disambiguationData":[TD([[makeQuery(id+"F6.imprint","IMPRINT",EDGE,{"derivedFrom":sQuery(id+"F6.wireOp",EDGE,"E47")}),-1.0]])]});
            cPlane(context, id + "F18", {"entities" : qUnion([Q0]), "cplaneType" : CPlaneType.OFFSET, "offset" : 7.14 * mm, "width" : 152.4 * mm, "height" : 152.4 * mm});
        }
        {
            var Q0;
            Q0=qCreatedBy(id+"F18.planeOp",FACE);
            var sketch = newSketch(context, id + "F19", { "sketchPlane" : qUnion([Q0])});
            skCircle(sketch, "E71", {"center": v(-67.76, 60.92) * mm, "radius": 2.8 * mm});
            skCircle(sketch, "E72.0", {"center": v(-67.76, 60.92) * mm, "radius": 3.18 * mm});
            skSolve(sketch);
        }
        {
            var Q0;
            Q0 = qSketchRegion(id + "F19", true);
            extrude(context, id + "F20", {"entities" : qUnion([Q0]), "operationType" : NewBodyOperationType.REMOVE, "depth" : 0.74 * mm});
        }
        {
            var Q0;
            Q0=makeQuery(id+"F11.opExtrude","CAP_FACE",FACE,{"disambiguationData":[OSD([sQuery(id+"F10.wireOp",EDGE,"E56.0.0"),sQuery(id+"F10.wireOp",EDGE,"E56.0.1"),sQuery(id+"F10.wireOp",EDGE,"E56.0.2"),sQuery(id+"F10.wireOp",EDGE,"E56.0.3"),sQuery(id+"F10.wireOp",EDGE,"E56.0.4"),sQuery(id+"F10.wireOp",EDGE,"E56.0.5"),sQuery(id+"F10.wireOp",EDGE,"E56.0.6"),sQuery(id+"F10.wireOp",EDGE,"E56.0.7"),sQuery(id+"F10.wireOp",EDGE,"E56.0.8"),sQuery(id+"F10.wireOp",EDGE,"E56.0.9"),sQuery(id+"F10.wireOp",EDGE,"E56.0.10"),sQuery(id+"F10.wireOp",EDGE,"E56.0.11"),sQuery(id+"F10.wireOp",EDGE,"E56.0.12"),sQuery(id+"F10.wireOp",EDGE,"E56.0.13"),sQuery(id+"F10.wireOp",EDGE,"E56.0.14"),sQuery(id+"F10.wireOp",EDGE,"E56.0.15"),sQuery(id+"F10.wireOp",EDGE,"E56.0.16"),sQuery(id+"F10.wireOp",EDGE,"E56.0.17"),sQuery(id+"F10.wireOp",EDGE,"E57.0"),sQuery(id+"F10.wireOp",EDGE,"E57.1"),sQuery(id+"F10.wireOp",EDGE,"E57.2"),sQuery(id+"F10.wireOp",EDGE,"E57.3"),sQuery(id+"F10.wireOp",EDGE,"E57.4"),sQuery(id+"F10.wireOp",EDGE,"E57.5"),sQuery(id+"F10.wireOp",EDGE,"E58.0")])],"isStart":false});
            var sketch = newSketch(context, id + "F21", { "sketchPlane" : qUnion([Q0])});
            skPoint(sketch, "E73.0", {"position": v(-67.76, 60.92) * mm});
            skPoint(sketch, "E73.1", {"position": v(-53.98, 25.4) * mm});
            skPoint(sketch, "E73.2", {"position": v(0, 25.4) * mm});
            skPoint(sketch, "E73.3", {"position": v(53.98, 25.4) * mm});
            skPoint(sketch, "E73.4", {"position": v(67.76, 60.92) * mm});
            skPoint(sketch, "E73.5", {"position": v(146.05, 79.38) * mm});
            skPoint(sketch, "E73.6", {"position": v(-146.05, 79.38) * mm});
            skPoint(sketch, "E74.0", {"position": v(0, 60.92) * mm});
            skSolve(sketch);
        }
        {
            var Q0;
            Q0=sQuery(id+"F0.wireOp",VERTEX,"E11.center");
            var Q1;
            Q1=sQuery(id+"F0.wireOp",VERTEX,"E19.center");
            var Q2;
            Q2=sQuery(id+"F0.wireOp",VERTEX,"E10.center");
            var Q3;
            Q3=sQuery(id+"F0.wireOp",VERTEX,"E9.center");
            var Q4;
            Q4=sQuery(id+"F0.wireOp",VERTEX,"E16.center");
            var Q5;
            Q5=sQuery(id+"F1.wireOp",VERTEX,"E27");
            var Q6;
            Q6=makeQuery(id+"F2.opExtrude","SWEPT_BODY",BODY,{"disambiguationData":[OSD([sQuery(id+"F1.wireOp",EDGE,"15da93e0-f6f9-46fd-b5b2-a4333d812dff"),sQuery(id+"F1.wireOp",EDGE,"16e28298-e9de-4e3e-a815-65364f24cef6"),sQuery(id+"F1.wireOp",EDGE,"E22"),sQuery(id+"F1.wireOp",EDGE,"E23"),sQuery(id+"F1.wireOp",EDGE,"E24"),sQuery(id+"F1.wireOp",EDGE,"E25"),sQuery(id+"F1.wireOp",EDGE,"E26"),sQuery(id+"F1.wireOp",EDGE,"859b3a9e-47a0-477d-ad96-80d0cd043ae0"),sQuery(id+"F1.wireOp",EDGE,"689f9d55-c2b5-4ecb-a3d1-7254dc2b26e6"),sQuery(id+"F1.wireOp",EDGE,"4789f967-c616-4e3b-9a4c-ef86a0a08756")])]});
            hole(context, id + "F22", {"style" : HoleStyle.C_SINK, "holeDiameter" : 3.45 * mm, "cSinkDiameter" : 7.8 * mm, "endStyle" : HoleEndStyle.THROUGH, "oppositeDirection" : true, "locations" : qUnion([Q0, Q1, Q2, Q3, Q4, Q5]), "scope" : qUnion([Q6]), "cSinkAngle" : 90 * degree});
        }
        {
            var Q0;
            Q0=sQuery(id+"F21.wireOp",VERTEX,"E73.0");
            var Q1;
            Q1=sQuery(id+"F21.wireOp",VERTEX,"E73.1");
            var Q2;
            Q2=sQuery(id+"F21.wireOp",VERTEX,"E73.2");
            var Q3;
            Q3=sQuery(id+"F21.wireOp",VERTEX,"E73.3");
            var Q4;
            Q4=sQuery(id+"F21.wireOp",VERTEX,"E73.4");
            var Q5;
            Q5=sQuery(id+"F21.wireOp",VERTEX,"E73.6");
            var Q6;
            Q6=sQuery(id+"F21.wireOp",VERTEX,"E73.5");
            var Q7;
            Q7=sQuery(id+"F21.wireOp",VERTEX,"E74.0");
            var Q8;
            Q8=makeQuery(id+"F11.opExtrude","SWEPT_BODY",BODY,{"disambiguationData":[OSD([sQuery(id+"F10.wireOp",EDGE,"E56.0.0"),sQuery(id+"F10.wireOp",EDGE,"E56.0.1"),sQuery(id+"F10.wireOp",EDGE,"E56.0.2"),sQuery(id+"F10.wireOp",EDGE,"E56.0.3"),sQuery(id+"F10.wireOp",EDGE,"E56.0.4"),sQuery(id+"F10.wireOp",EDGE,"E56.0.5"),sQuery(id+"F10.wireOp",EDGE,"E56.0.6"),sQuery(id+"F10.wireOp",EDGE,"E56.0.7"),sQuery(id+"F10.wireOp",EDGE,"E56.0.8"),sQuery(id+"F10.wireOp",EDGE,"E56.0.9"),sQuery(id+"F10.wireOp",EDGE,"E56.0.10"),sQuery(id+"F10.wireOp",EDGE,"E56.0.11"),sQuery(id+"F10.wireOp",EDGE,"E56.0.12"),sQuery(id+"F10.wireOp",EDGE,"E56.0.13"),sQuery(id+"F10.wireOp",EDGE,"E56.0.14"),sQuery(id+"F10.wireOp",EDGE,"E56.0.15"),sQuery(id+"F10.wireOp",EDGE,"E56.0.16"),sQuery(id+"F10.wireOp",EDGE,"E56.0.17"),sQuery(id+"F10.wireOp",EDGE,"E57.0"),sQuery(id+"F10.wireOp",EDGE,"E57.1"),sQuery(id+"F10.wireOp",EDGE,"E57.2"),sQuery(id+"F10.wireOp",EDGE,"E57.3"),sQuery(id+"F10.wireOp",EDGE,"E57.4"),sQuery(id+"F10.wireOp",EDGE,"E57.5"),sQuery(id+"F10.wireOp",EDGE,"E58.0")])]});
            hole(context, id + "F23", {"style" : HoleStyle.C_SINK, "holeDiameter" : 3.45 * mm, "cSinkDiameter" : 7.8 * mm, "endStyle" : HoleEndStyle.THROUGH, "locations" : qUnion([Q0, Q1, Q2, Q3, Q4, Q5, Q6, Q7]), "scope" : qUnion([Q8]), "cSinkAngle" : 90 * degree});
        }
        {
            var Q0;
            Q0=makeQuery(id+"F2.opExtrude","SWEPT_FACE",FACE,{"disambiguationData":[OSD([sQuery(id+"F1.wireOp",EDGE,"E30")])]});
            var sketch = newSketch(context, id + "F24", { "sketchPlane" : qUnion([Q0])});
            skLineSegment(sketch, "E75.bottom", {"start": v(0, 92.08) * mm, "end": v(44.45, 92.08) * mm});
            skLineSegment(sketch, "E75.top", {"start": v(0, 38.1) * mm, "end": v(44.45, 38.1) * mm});
            skLineSegment(sketch, "E75.left", {"start": v(0, 92.08) * mm, "end": v(0, 38.1) * mm});
            skLineSegment(sketch, "E75.right", {"start": v(44.45, 92.08) * mm, "end": v(44.45, 38.1) * mm});
            skPoint(sketch, "E76", {"position": v(8.33, 87.31) * mm});
            skPoint(sketch, "E77", {"position": v(8.33, 42.86) * mm});
            skPoint(sketch, "E78", {"position": v(36.12, 42.86) * mm});
            skPoint(sketch, "E79", {"position": v(36.12, 87.31) * mm});
            skLineSegment(sketch, "E80", {"start": v(22.22, 92.08) * mm, "end": v(22.23, 38.1) * mm, "construction": true});
            skLineSegment(sketch, "E81", {"start": v(44.45, 65.09) * mm, "end": v(0, 65.09) * mm, "construction": true});
            skSolve(sketch);
        }
        {
            var Q0;
            Q0 = qSketchRegion(id + "F24", true);
            extrude(context, id + "F25", {"entities" : qUnion([Q0]), "depth" : 3.17 * mm});
        }
        {
            var Q0;
            Q0=makeQuery(id+"F25.opExtrude","CAP_FACE",FACE,{"disambiguationData":[OSD([sQuery(id+"F24.wireOp",EDGE,"E75.bottom"),sQuery(id+"F24.wireOp",EDGE,"E75.top"),sQuery(id+"F24.wireOp",EDGE,"E75.left"),sQuery(id+"F24.wireOp",EDGE,"E75.right")])],"isStart":false});
            var sketch = newSketch(context, id + "F26", { "sketchPlane" : qUnion([Q0])});
            skPoint(sketch, "E82.0", {"position": v(8.33, 87.31) * mm});
            skPoint(sketch, "E82.1", {"position": v(36.12, 87.31) * mm});
            skPoint(sketch, "E82.2", {"position": v(36.12, 42.86) * mm});
            skPoint(sketch, "E82.3", {"position": v(8.33, 42.86) * mm});
            skSolve(sketch);
        }
        {
            var Q0;
            Q0=sQuery(id+"F26.wireOp",VERTEX,"E82.0");
            var Q1;
            Q1=sQuery(id+"F26.wireOp",VERTEX,"E82.3");
            var Q2;
            Q2=sQuery(id+"F26.wireOp",VERTEX,"E82.2");
            var Q3;
            Q3=sQuery(id+"F26.wireOp",VERTEX,"E82.1");
            var Q4;
            Q4=makeQuery(id+"F25.opExtrude","SWEPT_BODY",BODY,{"disambiguationData":[OSD([sQuery(id+"F24.wireOp",EDGE,"E75.bottom"),sQuery(id+"F24.wireOp",EDGE,"E75.top"),sQuery(id+"F24.wireOp",EDGE,"E75.left"),sQuery(id+"F24.wireOp",EDGE,"E75.right")])]});
            hole(context, id + "F27", {"style" : HoleStyle.C_SINK, "holeDiameter" : 2.87 * mm, "cSinkDiameter" : 6.48 * mm, "endStyle" : HoleEndStyle.THROUGH, "locations" : qUnion([Q0, Q1, Q2, Q3]), "scope" : qUnion([Q4]), "cSinkAngle" : 90 * degree});
        }
        {
            var Q0;
            {var subQ7=sQuery(id+"F1.wireOp",EDGE,"E30");Q0=makeQuery(id+"F13.imprint","IMPRINT",FACE,{"disambiguationData":[TD([[makeQuery(id+"F13.imprint","IMPRINT",EDGE,{"derivedFrom":makeQuery(id+"F2.opExtrude","CAP_EDGE",EDGE,{"disambiguationData":[OSD([subQ7])],"isStart":true})}),1.0]])]});}
            var sketch = newSketch(context, id + "F28", { "sketchPlane" : qUnion([Q0])});
            skLineSegment(sketch, "E83.bottom", {"start": v(-195.26, 31.75) * mm, "end": v(195.26, 31.75) * mm});
            skLineSegment(sketch, "E83.top", {"start": v(-195.26, 33.34) * mm, "end": v(195.26, 33.34) * mm});
            skLineSegment(sketch, "E83.left", {"start": v(-195.26, 31.75) * mm, "end": v(-195.26, 33.34) * mm});
            skLineSegment(sketch, "E83.right", {"start": v(195.26, 31.75) * mm, "end": v(195.26, 33.34) * mm});
            skLineSegment(sketch, "E84.bottom", {"start": v(195.26, 31.75) * mm, "end": v(198.44, 31.75) * mm});
            skLineSegment(sketch, "E84.top", {"start": v(195.26, 92.08) * mm, "end": v(198.44, 92.08) * mm});
            skLineSegment(sketch, "E84.left", {"start": v(195.26, 31.75) * mm, "end": v(195.26, 92.08) * mm});
            skLineSegment(sketch, "E84.right", {"start": v(198.44, 31.75) * mm, "end": v(198.44, 92.08) * mm});
            skSolve(sketch);
        }
        {
            var Q0;
            {var subQ3=sQuery(id+"F28.wireOp",EDGE,"E84.bottom");Q0=makeQuery(id+"F28.imprint","IMPRINT",FACE,{"disambiguationData":[TD([[makeQuery(id+"F28.imprint","IMPRINT",EDGE,{"derivedFrom":subQ3}),1.0]])]});}
            extrude(context, id + "F29", {"entities" : qUnion([Q0]), "depth" : 361.95 * mm});
        }
        {
            var Q0;
            {var subQ3=sQuery(id+"F28.wireOp",EDGE,"E83.top");Q0=makeQuery(id+"F28.imprint","IMPRINT",FACE,{"disambiguationData":[TD([[makeQuery(id+"F28.imprint","IMPRINT",EDGE,{"derivedFrom":subQ3}),-1.0]])]});}
            var Q1;
            Q1=makeQuery(id+"F29.opExtrude","CAP_FACE",FACE,{"disambiguationData":[OSD([sQuery(id+"F28.wireOp",EDGE,"E84.bottom"),sQuery(id+"F28.wireOp",EDGE,"E84.top"),sQuery(id+"F28.wireOp",EDGE,"E84.left"),sQuery(id+"F28.wireOp",EDGE,"E84.right")])],"isStart":false});
            extrude(context, id + "F30", {"entities" : qUnion([Q0]), "endBound" : BoundingType.UP_TO_SURFACE, "endBoundEntityFace" : qUnion([Q1]), "depth" : 25.4 * mm});
        }
        {
            var Q0;
            Q0=makeQuery(id+"F11.opExtrude","CAP_FACE",FACE,{"disambiguationData":[OSD([sQuery(id+"F10.wireOp",EDGE,"E56.0.5"),sQuery(id+"F10.wireOp",EDGE,"E56.0.6"),sQuery(id+"F10.wireOp",EDGE,"E56.0.7"),sQuery(id+"F10.wireOp",EDGE,"E56.0.8"),sQuery(id+"F10.wireOp",EDGE,"E56.0.9"),sQuery(id+"F10.wireOp",EDGE,"E56.0.10"),sQuery(id+"F10.wireOp",EDGE,"E56.0.11"),sQuery(id+"F10.wireOp",EDGE,"E56.0.12"),sQuery(id+"F10.wireOp",EDGE,"E57.0"),sQuery(id+"F10.wireOp",EDGE,"E57.1"),sQuery(id+"F10.wireOp",EDGE,"E57.2"),sQuery(id+"F10.wireOp",EDGE,"E57.3"),sQuery(id+"F10.wireOp",EDGE,"E57.4"),sQuery(id+"F10.wireOp",EDGE,"E57.5"),sQuery(id+"F10.wireOp",EDGE,"E58.0"),sQuery(id+"F10.wireOp",EDGE,"E59.0"),sQuery(id+"F10.wireOp",EDGE,"E59.1"),sQuery(id+"F10.wireOp",EDGE,"E59.3"),sQuery(id+"F10.wireOp",EDGE,"E59.5"),sQuery(id+"F10.wireOp",EDGE,"E59.6"),sQuery(id+"F10.wireOp",EDGE,"E59.8"),sQuery(id+"F10.wireOp",EDGE,"E59.9"),sQuery(id+"F10.wireOp",EDGE,"E59.10"),sQuery(id+"F10.wireOp",EDGE,"E60.0"),sQuery(id+"F10.wireOp",EDGE,"E60.1"),sQuery(id+"F10.wireOp",EDGE,"E60.2"),sQuery(id+"F10.wireOp",EDGE,"E61.0"),sQuery(id+"F10.wireOp",EDGE,"E61.1"),sQuery(id+"F10.wireOp",EDGE,"E61.2"),sQuery(id+"F10.wireOp",EDGE,"E61.3"),sQuery(id+"F10.wireOp",EDGE,"E61.4"),sQuery(id+"F10.wireOp",EDGE,"E61.5"),sQuery(id+"F10.wireOp",EDGE,"E59.12"),sQuery(id+"F10.wireOp",EDGE,"E62.0"),sQuery(id+"F10.wireOp",EDGE,"E62.1")])],"isStart":false});
            var sketch = newSketch(context, id + "F31", { "sketchPlane" : qUnion([Q0])});
            skPoint(sketch, "E85", {"position": v(-217.49, 87.31) * mm});
            skPoint(sketch, "E86", {"position": v(-217.49, 42.86) * mm});
            skPoint(sketch, "E87.0", {"position": v(-223.84, 87.31) * mm});
            skPoint(sketch, "E88.0", {"position": v(-223.84, 42.86) * mm});
            skPoint(sketch, "E89.MirrorP", {"position": v(217.49, 42.86) * mm});
            skPoint(sketch, "E90.MirrorP", {"position": v(217.49, 87.31) * mm});
            skSolve(sketch);
        }
        {
            var Q0;
            Q0=sQuery(id+"F31.wireOp",VERTEX,"E85");
            var Q1;
            Q1=sQuery(id+"F31.wireOp",VERTEX,"E86");
            var Q2;
            Q2=sQuery(id+"F31.wireOp",VERTEX,"E90.MirrorP");
            var Q3;
            Q3=sQuery(id+"F31.wireOp",VERTEX,"E89.MirrorP");
            var Q4;
            Q4=makeQuery(id+"F11.opExtrude","SWEPT_BODY",BODY,{"disambiguationData":[OSD([sQuery(id+"F10.wireOp",EDGE,"E56.0.5"),sQuery(id+"F10.wireOp",EDGE,"E56.0.6"),sQuery(id+"F10.wireOp",EDGE,"E56.0.7"),sQuery(id+"F10.wireOp",EDGE,"E56.0.8"),sQuery(id+"F10.wireOp",EDGE,"E56.0.9"),sQuery(id+"F10.wireOp",EDGE,"E56.0.10"),sQuery(id+"F10.wireOp",EDGE,"E56.0.11"),sQuery(id+"F10.wireOp",EDGE,"E56.0.12"),sQuery(id+"F10.wireOp",EDGE,"E57.0"),sQuery(id+"F10.wireOp",EDGE,"E57.1"),sQuery(id+"F10.wireOp",EDGE,"E57.2"),sQuery(id+"F10.wireOp",EDGE,"E57.3"),sQuery(id+"F10.wireOp",EDGE,"E57.4"),sQuery(id+"F10.wireOp",EDGE,"E57.5"),sQuery(id+"F10.wireOp",EDGE,"E58.0"),sQuery(id+"F10.wireOp",EDGE,"E59.0"),sQuery(id+"F10.wireOp",EDGE,"E59.1"),sQuery(id+"F10.wireOp",EDGE,"E59.3"),sQuery(id+"F10.wireOp",EDGE,"E59.5"),sQuery(id+"F10.wireOp",EDGE,"E59.6"),sQuery(id+"F10.wireOp",EDGE,"E59.8"),sQuery(id+"F10.wireOp",EDGE,"E59.9"),sQuery(id+"F10.wireOp",EDGE,"E59.10"),sQuery(id+"F10.wireOp",EDGE,"E60.0"),sQuery(id+"F10.wireOp",EDGE,"E60.1"),sQuery(id+"F10.wireOp",EDGE,"E60.2"),sQuery(id+"F10.wireOp",EDGE,"E61.0"),sQuery(id+"F10.wireOp",EDGE,"E61.1"),sQuery(id+"F10.wireOp",EDGE,"E61.2"),sQuery(id+"F10.wireOp",EDGE,"E61.3"),sQuery(id+"F10.wireOp",EDGE,"E61.4"),sQuery(id+"F10.wireOp",EDGE,"E61.5"),sQuery(id+"F10.wireOp",EDGE,"E59.12"),sQuery(id+"F10.wireOp",EDGE,"E62.0"),sQuery(id+"F10.wireOp",EDGE,"E62.1")])]});
            hole(context, id + "F32", {"style" : HoleStyle.C_SINK, "holeDiameter" : 2.87 * mm, "cSinkDiameter" : 6.48 * mm, "endStyle" : HoleEndStyle.THROUGH, "locations" : qUnion([Q0, Q1, Q2, Q3]), "scope" : qUnion([Q4]), "cSinkAngle" : 90 * degree});
        }
        {
            var Q0;
            {var subQ7=sQuery(id+"F1.wireOp",EDGE,"E30");Q0=makeQuery(id+"F13.imprint","IMPRINT",FACE,{"disambiguationData":[TD([[makeQuery(id+"F13.imprint","IMPRINT",EDGE,{"derivedFrom":makeQuery(id+"F2.opExtrude","CAP_EDGE",EDGE,{"disambiguationData":[OSD([subQ7])],"isStart":true})}),1.0]])]});}
            var sketch = newSketch(context, id + "F33", { "sketchPlane" : qUnion([Q0])});
            skPoint(sketch, "E91.0", {"position": v(217.49, 87.31) * mm});
            skPoint(sketch, "E91.1", {"position": v(217.49, 42.86) * mm});
            skPoint(sketch, "E91.2", {"position": v(-217.49, 42.86) * mm});
            skPoint(sketch, "E91.3", {"position": v(-217.49, 87.31) * mm});
            skSolve(sketch);
        }
        {
            var Q0;
            Q0=sQuery(id+"F33.wireOp",VERTEX,"E91.3");
            var Q1;
            Q1=sQuery(id+"F33.wireOp",VERTEX,"E91.2");
            var Q2;
            Q2=sQuery(id+"F33.wireOp",VERTEX,"E91.0");
            var Q3;
            Q3=sQuery(id+"F33.wireOp",VERTEX,"E91.1");
            var Q4;
            Q4=makeQuery(id+"F2.opExtrude","SWEPT_BODY",BODY,{"disambiguationData":[OSD([sQuery(id+"F1.wireOp",EDGE,"E22"),sQuery(id+"F1.wireOp",EDGE,"E23"),sQuery(id+"F1.wireOp",EDGE,"E24"),sQuery(id+"F1.wireOp",EDGE,"E25"),sQuery(id+"F1.wireOp",EDGE,"E26"),sQuery(id+"F1.wireOp",EDGE,"E28"),sQuery(id+"F1.wireOp",EDGE,"E29"),sQuery(id+"F1.wireOp",EDGE,"E30"),sQuery(id+"F1.wireOp",EDGE,"E31"),sQuery(id+"F1.wireOp",EDGE,"E32"),sQuery(id+"F1.wireOp",EDGE,"E33.trimOffspring"),sQuery(id+"F1.wireOp",EDGE,"E34.trimOffspring"),sQuery(id+"F1.wireOp",EDGE,"E36.trimOffspring"),sQuery(id+"F1.wireOp",EDGE,"E37.trimOffspring"),sQuery(id+"F1.wireOp",EDGE,"E38"),sQuery(id+"F1.wireOp",EDGE,"E39"),sQuery(id+"F1.wireOp",EDGE,"E40.trimOffspring"),sQuery(id+"F1.wireOp",EDGE,"E41.trimOffspring"),sQuery(id+"F1.wireOp",EDGE,"E42"),sQuery(id+"F1.wireOp",EDGE,"E43"),sQuery(id+"F1.wireOp",EDGE,"E44"),sQuery(id+"F1.wireOp",EDGE,"E45")])]});
            hole(context, id + "F34", {"style" : HoleStyle.SIMPLE, "holeDiameter" : 2.92 * mm, "endStyle" : HoleEndStyle.THROUGH, "locations" : qUnion([Q0, Q1, Q2, Q3]), "scope" : qUnion([Q4])});
        }
        {
            var Q0;
            Q0=sQuery(id+"F33.wireOp",VERTEX,"E91.0");
            var Q1;
            Q1=sQuery(id+"F33.wireOp",VERTEX,"E91.1");
            var Q2;
            Q2=sQuery(id+"F33.wireOp",VERTEX,"E91.3");
            var Q3;
            Q3=sQuery(id+"F33.wireOp",VERTEX,"E91.2");
            var Q4;
            Q4=makeQuery(id+"F2.opExtrude","SWEPT_BODY",BODY,{"disambiguationData":[OSD([sQuery(id+"F1.wireOp",EDGE,"E22"),sQuery(id+"F1.wireOp",EDGE,"E23"),sQuery(id+"F1.wireOp",EDGE,"E24"),sQuery(id+"F1.wireOp",EDGE,"E25"),sQuery(id+"F1.wireOp",EDGE,"E26"),sQuery(id+"F1.wireOp",EDGE,"E28"),sQuery(id+"F1.wireOp",EDGE,"E29"),sQuery(id+"F1.wireOp",EDGE,"E30"),sQuery(id+"F1.wireOp",EDGE,"E31"),sQuery(id+"F1.wireOp",EDGE,"E32"),sQuery(id+"F1.wireOp",EDGE,"E33.trimOffspring"),sQuery(id+"F1.wireOp",EDGE,"E34.trimOffspring"),sQuery(id+"F1.wireOp",EDGE,"E36.trimOffspring"),sQuery(id+"F1.wireOp",EDGE,"E37.trimOffspring"),sQuery(id+"F1.wireOp",EDGE,"E38"),sQuery(id+"F1.wireOp",EDGE,"E39"),sQuery(id+"F1.wireOp",EDGE,"E40.trimOffspring"),sQuery(id+"F1.wireOp",EDGE,"E41.trimOffspring"),sQuery(id+"F1.wireOp",EDGE,"E42"),sQuery(id+"F1.wireOp",EDGE,"E43"),sQuery(id+"F1.wireOp",EDGE,"E44"),sQuery(id+"F1.wireOp",EDGE,"E45")])]});
            hole(context, id + "F35", {"style" : HoleStyle.C_SINK, "holeDiameter" : 2.87 * mm, "cSinkDiameter" : 6.48 * mm, "endStyle" : HoleEndStyle.THROUGH, "locations" : qUnion([Q0, Q1, Q2, Q3]), "scope" : qUnion([Q4]), "cSinkAngle" : 90 * degree});
        }
        {
            var Q0;
            {var subQ7=sQuery(id+"F1.wireOp",EDGE,"E30");Q0=makeQuery(id+"F13.imprint","IMPRINT",FACE,{"disambiguationData":[TD([[makeQuery(id+"F13.imprint","IMPRINT",EDGE,{"derivedFrom":makeQuery(id+"F2.opExtrude","CAP_EDGE",EDGE,{"disambiguationData":[OSD([subQ7])],"isStart":true})}),1.0]])]});}
            var sketch = newSketch(context, id + "F36", { "sketchPlane" : qUnion([Q0])});
            skArc(sketch, "E92", {"start": v(209.89, 92.08) * mm, "mid": v(146.05, 144.46) * mm, "end": v(82.21, 92.07) * mm});
            skArc(sketch, "E93.0", {"start": v(203.4, 92.08) * mm, "mid": v(184.05, 124.17) * mm, "end": v(149.23, 138.03) * mm});
            skLineSegment(sketch, "E94", {"start": v(146.05, 79.38) * mm, "end": v(146.05, 138.11) * mm, "construction": true});
            skArc(sketch, "E95.0", {"start": v(142.88, 104.58) * mm, "mid": v(146.05, 104.78) * mm, "end": v(149.23, 104.58) * mm});
            skLineSegment(sketch, "E96.0", {"start": v(149.23, 104.58) * mm, "end": v(149.23, 138.03) * mm});
            skLineSegment(sketch, "E97.0", {"start": v(142.88, 104.58) * mm, "end": v(142.88, 138.03) * mm});
            skPoint(sketch, "E98.orphan", {"position": v(126.46, 95.54) * mm});
            skPoint(sketch, "E99.orphan", {"position": v(165.64, 95.54) * mm});
            skArc(sketch, "E100.trimOffspring", {"start": v(142.88, 138.03) * mm, "mid": v(108.05, 124.17) * mm, "end": v(88.7, 92.08) * mm});
            skLineSegment(sketch, "E101", {"start": v(82.21, 92.08) * mm, "end": v(88.7, 92.08) * mm});
            skLineSegment(sketch, "E102", {"start": v(203.4, 92.08) * mm, "end": v(209.89, 92.08) * mm});
            skLineSegment(sketch, "E103.MirrorCS", {"start": v(-142.88, 104.58) * mm, "end": v(-142.88, 138.03) * mm});
            skArc(sketch, "E104.MirrorCS", {"start": v(-209.89, 92.08) * mm, "mid": v(-146.05, 144.46) * mm, "end": v(-82.21, 92.07) * mm});
            skArc(sketch, "E105.MirrorCS", {"start": v(-203.4, 92.08) * mm, "mid": v(-184.05, 124.17) * mm, "end": v(-149.23, 138.03) * mm});
            skLineSegment(sketch, "E106.MirrorCS", {"start": v(-149.23, 104.58) * mm, "end": v(-149.23, 138.03) * mm});
            skArc(sketch, "E107.MirrorCS", {"start": v(-142.88, 138.03) * mm, "mid": v(-108.05, 124.17) * mm, "end": v(-88.7, 92.08) * mm});
            skLineSegment(sketch, "E108.MirrorCS", {"start": v(-82.21, 92.08) * mm, "end": v(-88.7, 92.08) * mm});
            skLineSegment(sketch, "E109.MirrorCS", {"start": v(-203.4, 92.08) * mm, "end": v(-209.89, 92.08) * mm});
            skArc(sketch, "E110.MirrorCS", {"start": v(-142.88, 104.58) * mm, "mid": v(-146.05, 104.78) * mm, "end": v(-149.23, 104.58) * mm});
            skPoint(sketch, "E111.MirrorP", {"position": v(-126.46, 95.54) * mm});
            skPoint(sketch, "E112.MirrorP", {"position": v(-165.64, 95.54) * mm});
            skSolve(sketch);
        }
        {
            var Q0;
            Q0 = qSketchRegion(id + "F36", true);
            var Q1;
            Q1=makeQuery(id+"F2.opExtrude","CAP_FACE",FACE,{"disambiguationData":[OSD([sQuery(id+"F1.wireOp",EDGE,"E22"),sQuery(id+"F1.wireOp",EDGE,"E23"),sQuery(id+"F1.wireOp",EDGE,"E24"),sQuery(id+"F1.wireOp",EDGE,"E25"),sQuery(id+"F1.wireOp",EDGE,"E26"),sQuery(id+"F1.wireOp",EDGE,"E28"),sQuery(id+"F1.wireOp",EDGE,"E29"),sQuery(id+"F1.wireOp",EDGE,"E30"),sQuery(id+"F1.wireOp",EDGE,"E31"),sQuery(id+"F1.wireOp",EDGE,"E32"),sQuery(id+"F1.wireOp",EDGE,"E33.trimOffspring"),sQuery(id+"F1.wireOp",EDGE,"E34.trimOffspring"),sQuery(id+"F1.wireOp",EDGE,"E36.trimOffspring"),sQuery(id+"F1.wireOp",EDGE,"E37.trimOffspring"),sQuery(id+"F1.wireOp",EDGE,"E38"),sQuery(id+"F1.wireOp",EDGE,"E39"),sQuery(id+"F1.wireOp",EDGE,"E40.trimOffspring"),sQuery(id+"F1.wireOp",EDGE,"E41.trimOffspring"),sQuery(id+"F1.wireOp",EDGE,"E42"),sQuery(id+"F1.wireOp",EDGE,"E43"),sQuery(id+"F1.wireOp",EDGE,"E44"),sQuery(id+"F1.wireOp",EDGE,"E45")])],"isStart":false});
            extrude(context, id + "F37", {"entities" : qUnion([Q0]), "operationType" : NewBodyOperationType.ADD, "endBound" : BoundingType.UP_TO_SURFACE, "oppositeDirection" : true, "endBoundEntityFace" : qUnion([Q1]), "depth" : 25.4 * mm});
        }
        {
            var Q0;
            Q0=makeQuery(id+"F37.opExtrude","SWEPT_EDGE",EDGE,{"disambiguationData":[OSD([sQuery(id+"F1.wireOp",EDGE,"E40.trimOffspring"),sQuery(id+"F36.wireOp",EDGE,"E107.MirrorCS"),sQuery(id+"F36.wireOp",EDGE,"E108.MirrorCS")])]});
            var Q1;
            Q1=makeQuery(id+"F37.opExtrude","SWEPT_EDGE",EDGE,{"disambiguationData":[OSD([sQuery(id+"F1.wireOp",EDGE,"E40.trimOffspring"),sQuery(id+"F36.wireOp",EDGE,"E104.MirrorCS"),sQuery(id+"F36.wireOp",EDGE,"E108.MirrorCS")])]});
            var Q2;
            Q2=makeQuery(id+"F37.opExtrude","SWEPT_EDGE",EDGE,{"disambiguationData":[OSD([sQuery(id+"F1.wireOp",EDGE,"E39"),sQuery(id+"F36.wireOp",EDGE,"E103.MirrorCS"),sQuery(id+"F36.wireOp",EDGE,"E110.MirrorCS")])]});
            var Q3;
            Q3=makeQuery(id+"F37.opExtrude","SWEPT_EDGE",EDGE,{"disambiguationData":[OSD([sQuery(id+"F36.wireOp",EDGE,"E103.MirrorCS"),sQuery(id+"F36.wireOp",EDGE,"E107.MirrorCS")])]});
            var Q4;
            Q4=makeQuery(id+"F37.opExtrude","SWEPT_EDGE",EDGE,{"disambiguationData":[OSD([sQuery(id+"F1.wireOp",EDGE,"E39"),sQuery(id+"F36.wireOp",EDGE,"E106.MirrorCS"),sQuery(id+"F36.wireOp",EDGE,"E110.MirrorCS")])]});
            var Q5;
            Q5=makeQuery(id+"F37.opExtrude","SWEPT_EDGE",EDGE,{"disambiguationData":[OSD([sQuery(id+"F36.wireOp",EDGE,"E105.MirrorCS"),sQuery(id+"F36.wireOp",EDGE,"E106.MirrorCS")])]});
            var Q6;
            Q6=makeQuery(id+"F37.opExtrude","SWEPT_EDGE",EDGE,{"disambiguationData":[OSD([sQuery(id+"F1.wireOp",EDGE,"E41.trimOffspring"),sQuery(id+"F36.wireOp",EDGE,"E105.MirrorCS"),sQuery(id+"F36.wireOp",EDGE,"E109.MirrorCS")])]});
            var Q7;
            Q7=makeQuery(id+"F37.opExtrude","SWEPT_EDGE",EDGE,{"disambiguationData":[OSD([sQuery(id+"F1.wireOp",EDGE,"E41.trimOffspring"),sQuery(id+"F36.wireOp",EDGE,"E104.MirrorCS"),sQuery(id+"F36.wireOp",EDGE,"E109.MirrorCS")])]});
            var Q8;
            Q8=makeQuery(id+"F37.opExtrude","SWEPT_EDGE",EDGE,{"disambiguationData":[OSD([sQuery(id+"F1.wireOp",EDGE,"E40.trimOffspring"),sQuery(id+"F36.wireOp",EDGE,"E92"),sQuery(id+"F36.wireOp",EDGE,"E101")])]});
            var Q9;
            Q9=makeQuery(id+"F37.opExtrude","SWEPT_EDGE",EDGE,{"disambiguationData":[OSD([sQuery(id+"F1.wireOp",EDGE,"E38"),sQuery(id+"F36.wireOp",EDGE,"E95.0"),sQuery(id+"F36.wireOp",EDGE,"E97.0")])]});
            var Q10;
            Q10=makeQuery(id+"F37.opExtrude","SWEPT_EDGE",EDGE,{"disambiguationData":[OSD([sQuery(id+"F1.wireOp",EDGE,"E38"),sQuery(id+"F36.wireOp",EDGE,"E95.0"),sQuery(id+"F36.wireOp",EDGE,"E96.0")])]});
            var Q11;
            Q11=makeQuery(id+"F37.opExtrude","SWEPT_EDGE",EDGE,{"disambiguationData":[OSD([sQuery(id+"F1.wireOp",EDGE,"E34.trimOffspring"),sQuery(id+"F36.wireOp",EDGE,"E92"),sQuery(id+"F36.wireOp",EDGE,"E102")])]});
            var Q12;
            Q12=makeQuery(id+"F37.opExtrude","SWEPT_EDGE",EDGE,{"disambiguationData":[OSD([sQuery(id+"F1.wireOp",EDGE,"E34.trimOffspring"),sQuery(id+"F36.wireOp",EDGE,"E93.0"),sQuery(id+"F36.wireOp",EDGE,"E102")])]});
            var Q13;
            Q13=makeQuery(id+"F37.opExtrude","SWEPT_EDGE",EDGE,{"disambiguationData":[OSD([sQuery(id+"F36.wireOp",EDGE,"E93.0"),sQuery(id+"F36.wireOp",EDGE,"E96.0")])]});
            var Q14;
            Q14=makeQuery(id+"F37.opExtrude","SWEPT_EDGE",EDGE,{"disambiguationData":[OSD([sQuery(id+"F36.wireOp",EDGE,"E97.0"),sQuery(id+"F36.wireOp",EDGE,"E100.trimOffspring")])]});
            fillet(context, id + "F38", {"entities" : qUnion([Q0, Q1, Q2, Q3, Q4, Q5, Q6, Q7, Q8, Q9, Q10, Q11, Q12, Q13, Q14]), "radius" : 9.52 * mm, "tangentPropagation" : true, "allowEdgeOverflow" : false});
        }
        {
            var Q0;
            Q0=makeQuery(id+"F29.opExtrude","SWEPT_FACE",FACE,{"disambiguationData":[OSD([sQuery(id+"F28.wireOp",EDGE,"E84.right")])]});
            var sketch = newSketch(context, id + "F39", { "sketchPlane" : qUnion([Q0])});
            skLineSegment(sketch, "E113", {"start": v(-180.98, 92.07) * mm, "end": v(-180.98, 31.75) * mm, "construction": true});
            skLineSegment(sketch, "E114", {"start": v(0, 61.91) * mm, "end": v(-361.95, 61.91) * mm, "construction": true});
            skPoint(sketch, "E115", {"position": v(-6.35, 87.31) * mm});
            skPoint(sketch, "E116", {"position": v(-6.35, 36.51) * mm});
            skPoint(sketch, "E117", {"position": v(-355.6, 87.31) * mm});
            skPoint(sketch, "E118", {"position": v(-355.6, 36.51) * mm});
            skSolve(sketch);
        }
        {
            var Q0;
            Q0=sQuery(id+"F39.wireOp",VERTEX,"E117");
            var Q1;
            Q1=sQuery(id+"F39.wireOp",VERTEX,"E118");
            var Q2;
            Q2=sQuery(id+"F39.wireOp",VERTEX,"E115");
            var Q3;
            Q3=sQuery(id+"F39.wireOp",VERTEX,"E116");
            var Q4;
            Q4=makeQuery(id+"F29.opExtrude","SWEPT_BODY",BODY,{"disambiguationData":[OSD([sQuery(id+"F28.wireOp",EDGE,"E84.bottom"),sQuery(id+"F28.wireOp",EDGE,"E84.top"),sQuery(id+"F28.wireOp",EDGE,"E84.left"),sQuery(id+"F28.wireOp",EDGE,"E84.right")])]});
            hole(context, id + "F40", {"style" : HoleStyle.C_SINK, "holeDiameter" : 2.87 * mm, "cSinkDiameter" : 6.48 * mm, "endStyle" : HoleEndStyle.THROUGH, "locations" : qUnion([Q0, Q1, Q2, Q3]), "scope" : qUnion([Q4]), "cSinkAngle" : 90 * degree});
        }
        {
            var Q0;
            Q0=makeQuery(id+"F37.boolean.opBoolean","MERGE",FACE,{"derivedFrom":[makeQuery(id+"F2.opExtrude","CAP_FACE",FACE,{"disambiguationData":[OSD([sQuery(id+"F1.wireOp",EDGE,"E22"),sQuery(id+"F1.wireOp",EDGE,"E23"),sQuery(id+"F1.wireOp",EDGE,"E24"),sQuery(id+"F1.wireOp",EDGE,"E25"),sQuery(id+"F1.wireOp",EDGE,"E26"),sQuery(id+"F1.wireOp",EDGE,"E28"),sQuery(id+"F1.wireOp",EDGE,"E29"),sQuery(id+"F1.wireOp",EDGE,"E30"),sQuery(id+"F1.wireOp",EDGE,"E31"),sQuery(id+"F1.wireOp",EDGE,"E32"),sQuery(id+"F1.wireOp",EDGE,"E33.trimOffspring"),sQuery(id+"F1.wireOp",EDGE,"E34.trimOffspring"),sQuery(id+"F1.wireOp",EDGE,"E36.trimOffspring"),sQuery(id+"F1.wireOp",EDGE,"E37.trimOffspring"),sQuery(id+"F1.wireOp",EDGE,"E38"),sQuery(id+"F1.wireOp",EDGE,"E39"),sQuery(id+"F1.wireOp",EDGE,"E40.trimOffspring"),sQuery(id+"F1.wireOp",EDGE,"E41.trimOffspring"),sQuery(id+"F1.wireOp",EDGE,"E42"),sQuery(id+"F1.wireOp",EDGE,"E43"),sQuery(id+"F1.wireOp",EDGE,"E44"),sQuery(id+"F1.wireOp",EDGE,"E45")])],"isStart":false}),makeQuery(id+"F37.opExtrude","CAP_FACE",FACE,{"disambiguationData":[OSD([sQuery(id+"F36.wireOp",EDGE,"E92"),sQuery(id+"F36.wireOp",EDGE,"E93.0"),sQuery(id+"F36.wireOp",EDGE,"E95.0"),sQuery(id+"F36.wireOp",EDGE,"E96.0"),sQuery(id+"F36.wireOp",EDGE,"E97.0"),sQuery(id+"F36.wireOp",EDGE,"E100.trimOffspring"),sQuery(id+"F36.wireOp",EDGE,"E101"),sQuery(id+"F36.wireOp",EDGE,"E102")])],"isStart":false}),makeQuery(id+"F37.opExtrude","CAP_FACE",FACE,{"disambiguationData":[OSD([sQuery(id+"F36.wireOp",EDGE,"E103.MirrorCS"),sQuery(id+"F36.wireOp",EDGE,"E104.MirrorCS"),sQuery(id+"F36.wireOp",EDGE,"E105.MirrorCS"),sQuery(id+"F36.wireOp",EDGE,"E106.MirrorCS"),sQuery(id+"F36.wireOp",EDGE,"E107.MirrorCS"),sQuery(id+"F36.wireOp",EDGE,"E108.MirrorCS"),sQuery(id+"F36.wireOp",EDGE,"E109.MirrorCS"),sQuery(id+"F36.wireOp",EDGE,"E110.MirrorCS")])],"isStart":false})]});
            var sketch = newSketch(context, id + "F41", { "sketchPlane" : qUnion([Q0])});
            skPoint(sketch, "E119.0", {"position": v(-198.44, 87.31) * mm});
            skPoint(sketch, "E119.1", {"position": v(-198.44, 36.51) * mm});
            skLineSegment(sketch, "E120.0", {"start": v(-195.26, 31.75) * mm, "end": v(-195.26, 92.08) * mm, "construction": true});
            skPoint(sketch, "E121", {"position": v(-190.1, 87.31) * mm});
            skPoint(sketch, "E122", {"position": v(-190.1, 36.51) * mm});
            skLineSegment(sketch, "E123", {"start": v(0, 0) * mm, "end": v(0, 92.08) * mm, "construction": true});
            skPoint(sketch, "E124.MirrorP", {"position": v(190.1, 36.51) * mm});
            skPoint(sketch, "E125.MirrorP", {"position": v(190.1, 87.31) * mm});
            skSolve(sketch);
        }
        {
            var Q0;
            Q0=sQuery(id+"F41.wireOp",VERTEX,"E121");
            var Q1;
            Q1=sQuery(id+"F41.wireOp",VERTEX,"E122");
            var Q2;
            Q2=sQuery(id+"F41.wireOp",VERTEX,"E125.MirrorP");
            var Q3;
            Q3=sQuery(id+"F41.wireOp",VERTEX,"E124.MirrorP");
            var Q4;
            Q4=makeQuery(id+"F2.opExtrude","SWEPT_BODY",BODY,{"disambiguationData":[OSD([sQuery(id+"F1.wireOp",EDGE,"E22"),sQuery(id+"F1.wireOp",EDGE,"E23"),sQuery(id+"F1.wireOp",EDGE,"E24"),sQuery(id+"F1.wireOp",EDGE,"E25"),sQuery(id+"F1.wireOp",EDGE,"E26"),sQuery(id+"F1.wireOp",EDGE,"E28"),sQuery(id+"F1.wireOp",EDGE,"E29"),sQuery(id+"F1.wireOp",EDGE,"E30"),sQuery(id+"F1.wireOp",EDGE,"E31"),sQuery(id+"F1.wireOp",EDGE,"E32"),sQuery(id+"F1.wireOp",EDGE,"E33.trimOffspring"),sQuery(id+"F1.wireOp",EDGE,"E34.trimOffspring"),sQuery(id+"F1.wireOp",EDGE,"E36.trimOffspring"),sQuery(id+"F1.wireOp",EDGE,"E37.trimOffspring"),sQuery(id+"F1.wireOp",EDGE,"E38"),sQuery(id+"F1.wireOp",EDGE,"E39"),sQuery(id+"F1.wireOp",EDGE,"E40.trimOffspring"),sQuery(id+"F1.wireOp",EDGE,"E41.trimOffspring"),sQuery(id+"F1.wireOp",EDGE,"E42"),sQuery(id+"F1.wireOp",EDGE,"E43"),sQuery(id+"F1.wireOp",EDGE,"E44"),sQuery(id+"F1.wireOp",EDGE,"E45")])]});
            hole(context, id + "F42", {"style" : HoleStyle.C_SINK, "holeDiameter" : 2.87 * mm, "cSinkDiameter" : 6.48 * mm, "endStyle" : HoleEndStyle.THROUGH, "locations" : qUnion([Q0, Q1, Q2, Q3]), "scope" : qUnion([Q4]), "cSinkAngle" : 90 * degree});
        }
        {
            var Q0;
            Q0=makeQuery(id+"F25.opExtrude","CAP_EDGE",EDGE,{"disambiguationData":[OSD([sQuery(id+"F24.wireOp",EDGE,"E75.left")])],"isStart":false});
            var Q1;
            Q1=makeQuery(id+"F25.opExtrude","CAP_EDGE",EDGE,{"disambiguationData":[OSD([sQuery(id+"F24.wireOp",EDGE,"E75.bottom")])],"isStart":false});
            var Q2;
            Q2=makeQuery(id+"F25.opExtrude","CAP_EDGE",EDGE,{"disambiguationData":[OSD([sQuery(id+"F24.wireOp",EDGE,"E75.right")])],"isStart":false});
            var Q3;
            Q3=makeQuery(id+"F25.opExtrude","CAP_EDGE",EDGE,{"disambiguationData":[OSD([sQuery(id+"F24.wireOp",EDGE,"E75.top")])],"isStart":false});
            chamfer(context, id + "F43", {"entities" : qUnion([Q0, Q1, Q2, Q3]), "width" : 0.64 * mm, "tangentPropagation" : true});
        }
        {
            var Q0;
            Q0=makeQuery(id+"F30.opExtrude","SWEPT_FACE",FACE,{"disambiguationData":[OSD([sQuery(id+"F28.wireOp",EDGE,"E83.top")])]});
            var sketch = newSketch(context, id + "F44", { "sketchPlane" : qUnion([Q0])});
            skLineSegment(sketch, "E126.0", {"start": v(0, -3.9) * mm, "end": v(0, 3.9) * mm});
            skLineSegment(sketch, "E127", {"start": v(0, 0) * mm, "end": v(-361.95, 0) * mm, "construction": true});
            skLineSegment(sketch, "E128.bottom", {"start": v(-107.95, -44.45) * mm, "end": v(0, -44.45) * mm});
            skLineSegment(sketch, "E128.top", {"start": v(-107.95, 44.45) * mm, "end": v(0, 44.45) * mm});
            skLineSegment(sketch, "E128.left", {"start": v(-107.95, -44.45) * mm, "end": v(-107.95, 44.45) * mm});
            skLineSegment(sketch, "E128.right", {"start": v(0, -44.45) * mm, "end": v(0, 44.45) * mm});
            skLineSegment(sketch, "E129.bottom", {"start": v(-361.95, -44.45) * mm, "end": v(-254, -44.45) * mm});
            skLineSegment(sketch, "E129.top", {"start": v(-361.95, 44.45) * mm, "end": v(-254, 44.45) * mm});
            skLineSegment(sketch, "E129.left", {"start": v(-361.95, -44.45) * mm, "end": v(-361.95, 44.45) * mm});
            skLineSegment(sketch, "E129.right", {"start": v(-254, -44.45) * mm, "end": v(-254, 44.45) * mm});
            skSolve(sketch);
        }
        {
            var Q0;
            {var subQ3=sQuery(id+"F44.wireOp",EDGE,"E128.bottom");Q0=makeQuery(id+"F44.imprint","IMPRINT",FACE,{"disambiguationData":[TD([[makeQuery(id+"F44.imprint","IMPRINT",EDGE,{"derivedFrom":subQ3}),1.0]])]});}
            var Q1;
            Q1=makeQuery(id+"F44.imprint","IMPRINT",FACE,{"disambiguationData":[TD([[makeQuery(id+"F44.imprint","IMPRINT",EDGE,{"derivedFrom":sQuery(id+"F44.wireOp",EDGE,"E129.bottom")}),1.0]])]});
            var Q2;
            Q2=makeQuery(id+"F30.opExtrude","SWEPT_FACE",FACE,{"disambiguationData":[OSD([sQuery(id+"F28.wireOp",EDGE,"E83.bottom")])]});
            extrude(context, id + "F45", {"entities" : qUnion([Q0, Q1]), "operationType" : NewBodyOperationType.REMOVE, "endBound" : BoundingType.UP_TO_SURFACE, "oppositeDirection" : true, "endBoundEntityFace" : qUnion([Q2]), "depth" : 25.4 * mm});
        }
        {
            var Q0;
            Q0=makeQuery(id+"F45.boolean.opBoolean","COPY",EDGE,{"derivedFrom":makeQuery(id+"F45.opExtrude","SWEPT_EDGE",EDGE,{"disambiguationData":[OSD([sQuery(id+"F44.wireOp",EDGE,"E129.bottom"),sQuery(id+"F44.wireOp",EDGE,"E129.right")])]})});
            var Q1;
            Q1=makeQuery(id+"F45.boolean.opBoolean","COPY",EDGE,{"derivedFrom":makeQuery(id+"F45.opExtrude","SWEPT_EDGE",EDGE,{"disambiguationData":[OSD([sQuery(id+"F44.wireOp",EDGE,"E129.top"),sQuery(id+"F44.wireOp",EDGE,"E129.right")])]})});
            var Q2;
            Q2=makeQuery(id+"F45.boolean.opBoolean","COPY",EDGE,{"derivedFrom":makeQuery(id+"F45.opExtrude","SWEPT_EDGE",EDGE,{"disambiguationData":[OSD([sQuery(id+"F44.wireOp",EDGE,"E128.top"),sQuery(id+"F44.wireOp",EDGE,"E128.left")])]})});
            var Q3;
            Q3=makeQuery(id+"F45.boolean.opBoolean","COPY",EDGE,{"derivedFrom":makeQuery(id+"F45.opExtrude","SWEPT_EDGE",EDGE,{"disambiguationData":[OSD([sQuery(id+"F44.wireOp",EDGE,"E128.bottom"),sQuery(id+"F44.wireOp",EDGE,"E128.left")])]})});
            fillet(context, id + "F46", {"entities" : qUnion([Q0, Q1, Q2, Q3]), "radius" : 6.35 * mm, "tangentPropagation" : true, "allowEdgeOverflow" : false});
        }
    });
